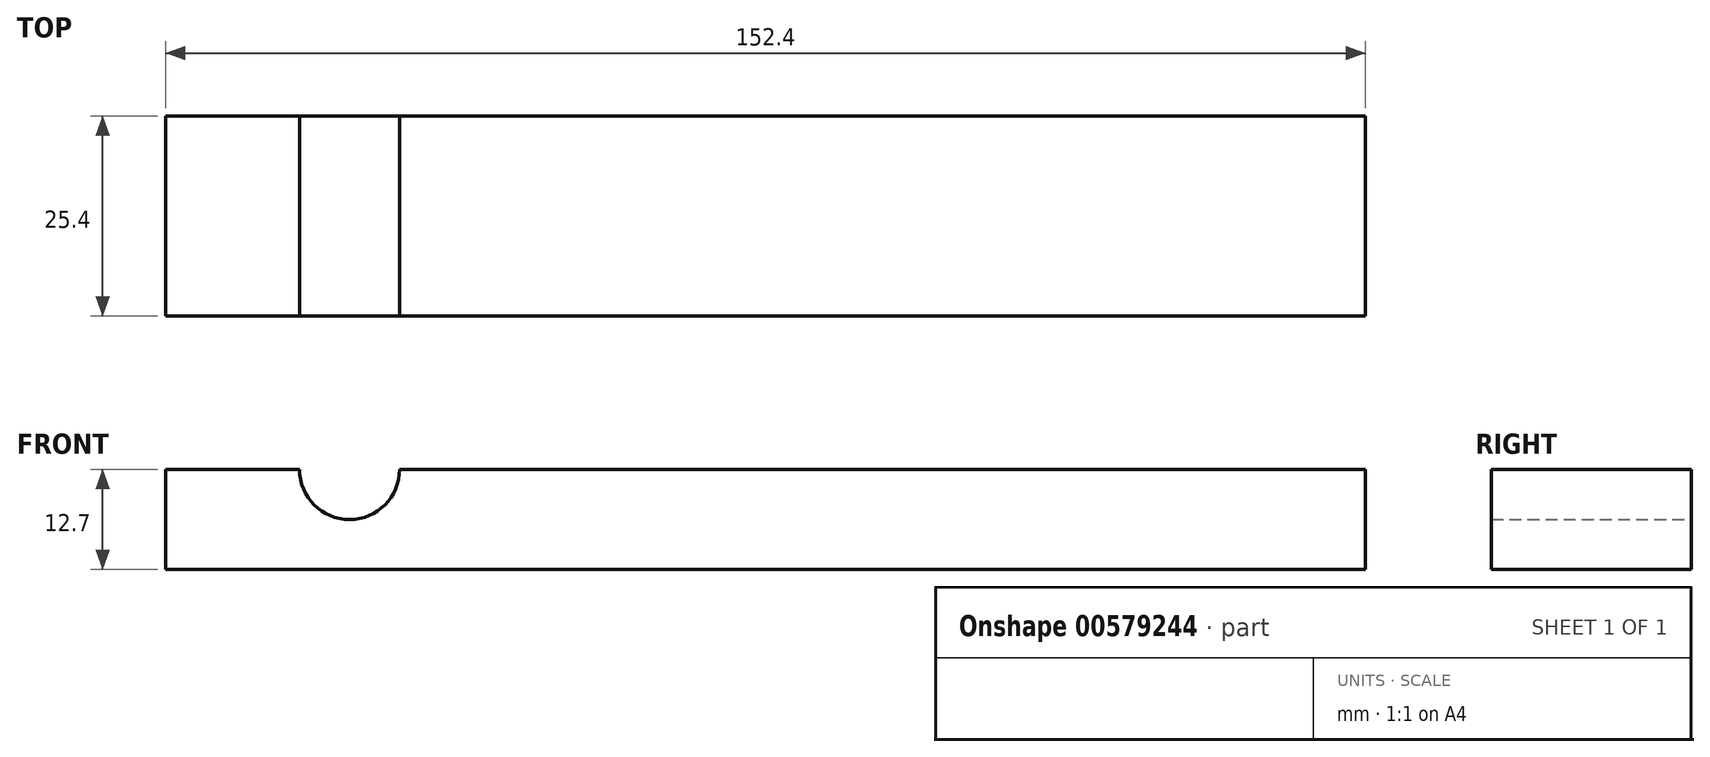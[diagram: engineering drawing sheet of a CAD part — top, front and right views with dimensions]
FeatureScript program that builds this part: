
annotation { "Feature Type Name" : "Feature", "Feature Type Description" : "" }
export const myFeature = defineFeature(function(context is Context, id is Id, definition is map)
    precondition{}
    {
        {
            var Q0;
            Q0=qCreatedBy(makeId("Front.planeOp"),FACE);
            var sketch = newSketch(context, id + "F0", { "sketchPlane" : qUnion([Q0])});
            skCircle(sketch, "E0", {"center": v(0, 0) * mm, "radius": 6.35 * mm});
            skLineSegment(sketch, "E1.bottom", {"start": v(-23.36, 0) * mm, "end": v(129.04, 0) * mm});
            skLineSegment(sketch, "E1.top", {"start": v(-23.36, -12.7) * mm, "end": v(129.04, -12.7) * mm});
            skLineSegment(sketch, "E1.left", {"start": v(-23.36, 0) * mm, "end": v(-23.36, -12.7) * mm});
            skLineSegment(sketch, "E1.right", {"start": v(129.04, 0) * mm, "end": v(129.04, -12.7) * mm});
            skSolve(sketch);
        }
        {
            var Q0;
            Q0=makeQuery(id+"F0.imprint","IMPRINT",FACE,{"disambiguationData":[TD([[makeQuery(id+"F0.imprint","IMPRINT",EDGE,{"derivedFrom":sQuery(id+"F0.wireOp",EDGE,"E1.top")}),1.0]])]});
            extrude(context, id + "F1", {"entities" : qUnion([Q0]), "depth" : 25.4 * mm, "offsetDistance" : 25.4 * mm});
        }
    });
